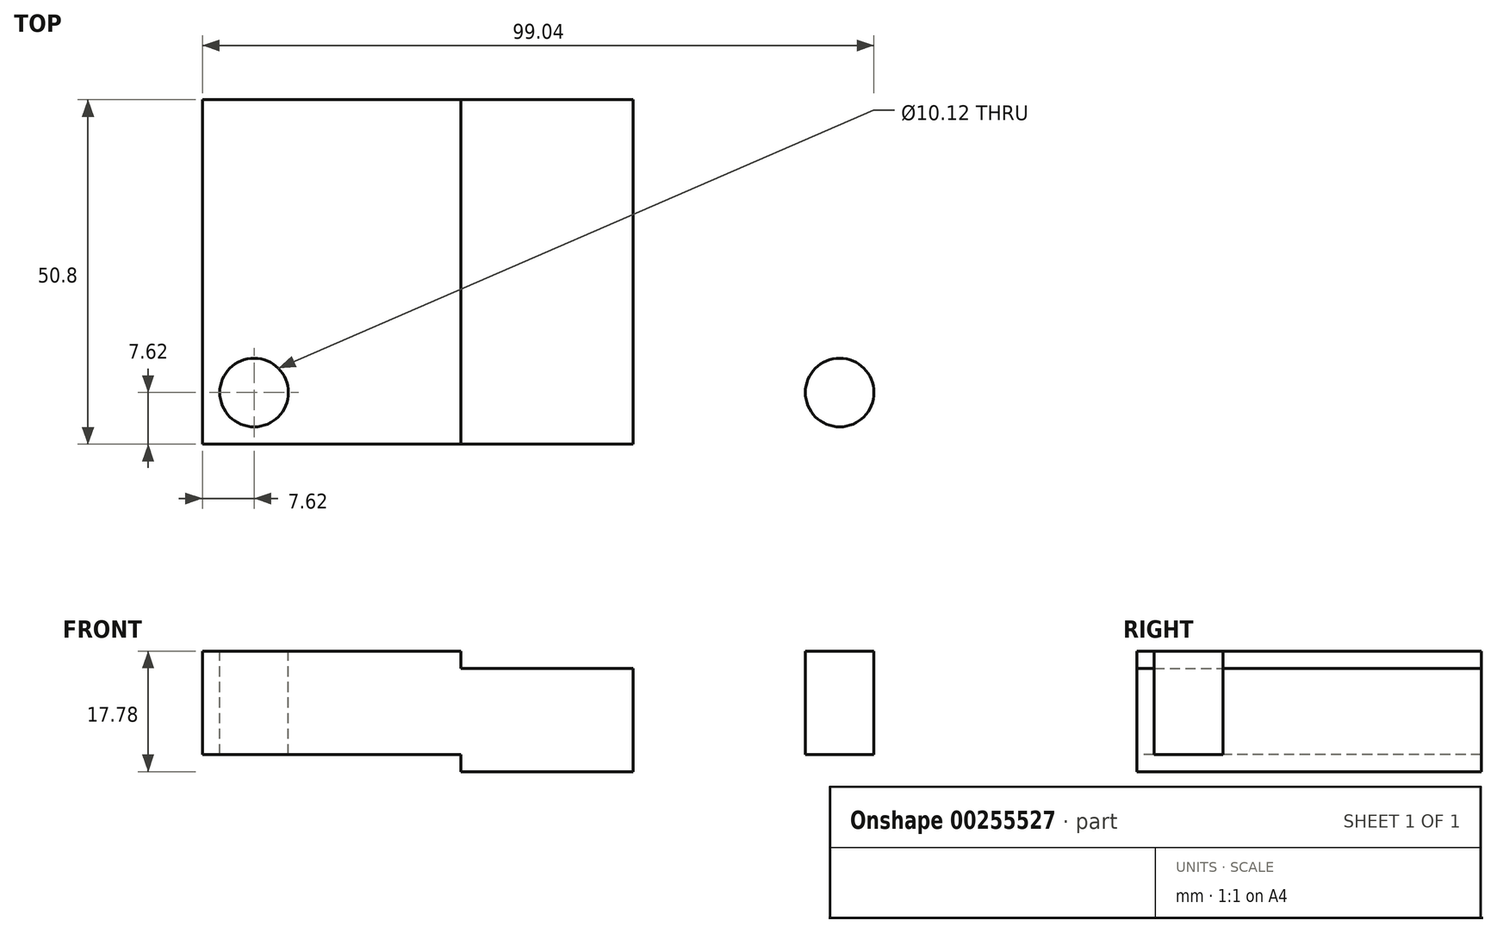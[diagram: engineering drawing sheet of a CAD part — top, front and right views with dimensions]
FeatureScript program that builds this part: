
annotation { "Feature Type Name" : "Feature", "Feature Type Description" : "" }
export const myFeature = defineFeature(function(context is Context, id is Id, definition is map)
    precondition{}
    {
        {
            var Q0;
            Q0=qCreatedBy(makeId("Top.planeOp"),FACE);
            var sketch = newSketch(context, id + "F0", { "sketchPlane" : qUnion([Q0])});
            skLineSegment(sketch, "E0.bottom", {"start": v(-50.8, 25.4) * mm, "end": v(50.8, 25.4) * mm});
            skLineSegment(sketch, "E0.top", {"start": v(-50.8, -25.4) * mm, "end": v(50.8, -25.4) * mm});
            skLineSegment(sketch, "E0.left", {"start": v(-50.8, 25.4) * mm, "end": v(-50.8, -25.4) * mm});
            skLineSegment(sketch, "E0.right", {"start": v(50.8, 25.4) * mm, "end": v(50.8, -25.4) * mm});
            skPoint(sketch, "E0.middle", {"position": v(0, 0) * mm});
            skLineSegment(sketch, "E1", {"start": v(-12.7, 25.4) * mm, "end": v(-12.7, -25.4) * mm});
            skLineSegment(sketch, "E2", {"start": v(12.7, 25.4) * mm, "end": v(12.7, -26.8) * mm});
            skSolve(sketch);
        }
        {
            var Q0;
            Q0 = qSketchRegion(id + "F0", true);
            extrude(context, id + "F1", {"entities" : qUnion([Q0]), "depth" : 12.7 * mm});
        }
        {
            var Q0;
            {var subQ0=sQuery(id+"F0.wireOp",EDGE,"E0.right");Q0=makeQuery(id+"F0.imprint","IMPRINT",FACE,{"disambiguationData":[TD([[makeQuery(id+"F0.imprint","IMPRINT",EDGE,{"derivedFrom":subQ0}),-1.0]])]});}
            var Q1;
            {var subQ0=sQuery(id+"F0.wireOp",EDGE,"E0.left");Q1=makeQuery(id+"F0.imprint","IMPRINT",FACE,{"disambiguationData":[TD([[makeQuery(id+"F0.imprint","IMPRINT",EDGE,{"derivedFrom":subQ0}),1.0]])]});}
            extrude(context, id + "F2", {"entities" : qUnion([Q0, Q1]), "operationType" : NewBodyOperationType.ADD, "depth" : 15.24 * mm});
        }
        {
            var Q0;
            Q0=makeQuery(id+"F1.opExtrude","CAP_FACE",FACE,{"disambiguationData":[OSD([sQuery(id+"F0.wireOp",EDGE,"E0.bottom"),sQuery(id+"F0.wireOp",EDGE,"E0.top"),sQuery(id+"F0.wireOp",EDGE,"E0.left"),sQuery(id+"F0.wireOp",EDGE,"E0.right")])],"isStart":true});
            var sketch = newSketch(context, id + "F3", { "sketchPlane" : qUnion([Q0])});
            skLineSegment(sketch, "E3", {"start": v(0, 0) * mm, "end": v(0, 25.4) * mm, "construction": true});
            skSolve(sketch);
        }
        {
            var Q0;
            Q0=sQuery(id+"F3.wireOp",VERTEX,"E3.end");
            var Q1;
            Q1=sQuery(id+"F3.wireOp",EDGE,"E3");
            cPlane(context, id + "F4", {"entities" : qUnion([Q0, Q1]), "cplaneType" : CPlaneType.LINE_POINT, "offset" : 25.4 * mm, "width" : 152.4 * mm, "height" : 152.4 * mm});
        }
        {
            var Q0;
            Q0=qCreatedBy(id+"F4.planeOp",FACE);
            var sketch = newSketch(context, id + "F5", { "sketchPlane" : qUnion([Q0])});
            skLineSegment(sketch, "E4", {"start": v(0, 0) * mm, "end": v(0, -2.54) * mm});
            skLineSegment(sketch, "E5", {"start": v(0, -2.54) * mm, "end": v(-12.7, -2.54) * mm});
            skLineSegment(sketch, "E6.MirrorCS", {"start": v(0, -2.54) * mm, "end": v(12.7, -2.54) * mm});
            skLineSegment(sketch, "E7", {"start": v(-12.7, -2.54) * mm, "end": v(-12.7, 0) * mm});
            skLineSegment(sketch, "E8", {"start": v(12.7, -2.54) * mm, "end": v(12.7, 0) * mm});
            skLineSegment(sketch, "E9", {"start": v(12.7, 0) * mm, "end": v(-12.7, 0) * mm});
            skSolve(sketch);
        }
        {
            var Q0;
            {var subQ0=sQuery(id+"F5.wireOp",EDGE,"E4");Q0=makeQuery(id+"F5.imprint","IMPRINT",FACE,{"disambiguationData":[TD([[makeQuery(id+"F5.imprint","IMPRINT",EDGE,{"derivedFrom":subQ0}),-1.0]])]});}
            var Q1;
            {var subQ0=sQuery(id+"F5.wireOp",EDGE,"E4");Q1=makeQuery(id+"F5.imprint","IMPRINT",FACE,{"disambiguationData":[TD([[makeQuery(id+"F5.imprint","IMPRINT",EDGE,{"derivedFrom":subQ0}),1.0]])]});}
            extrude(context, id + "F6", {"entities" : qUnion([Q0, Q1]), "operationType" : NewBodyOperationType.ADD, "oppositeDirection" : true, "depth" : 50.8 * mm});
        }
        {
            var Q0;
            Q0=makeQuery(id+"F2.opExtrude","CAP_FACE",FACE,{"disambiguationData":[OSD([sQuery(id+"F0.wireOp",EDGE,"E0.bottom"),sQuery(id+"F0.wireOp",EDGE,"E0.top"),sQuery(id+"F0.wireOp",EDGE,"E0.right"),sQuery(id+"F0.wireOp",EDGE,"E2")])],"isStart":false});
            var sketch = newSketch(context, id + "F7", { "sketchPlane" : qUnion([Q0])});
            skLineSegment(sketch, "E10", {"start": v(50.8, 25.4) * mm, "end": v(43.18, 25.4) * mm});
            skLineSegment(sketch, "E11", {"start": v(43.18, 25.4) * mm, "end": v(43.18, 17.78) * mm});
            skCircle(sketch, "E12", {"center": v(43.18, 17.78) * mm, "radius": 5.06 * mm});
            skCircle(sketch, "E13.MirrorC", {"center": v(43.18, -17.78) * mm, "radius": 5.06 * mm});
            skCircle(sketch, "E14.MirrorC", {"center": v(-43.18, -17.78) * mm, "radius": 5.06 * mm});
            skCircle(sketch, "E15.MirrorC", {"center": v(-43.18, 17.78) * mm, "radius": 5.06 * mm});
            skSolve(sketch);
        }
        {
            var Q0;
            Q0=makeQuery(id+"F7.imprint","IMPRINT",FACE,{"disambiguationData":[TD([[makeQuery(id+"F7.imprint","IMPRINT",EDGE,{"derivedFrom":sQuery(id+"F7.wireOp",EDGE,"E12")}),1.0]])]});
            var Q1;
            Q1=makeQuery(id+"F7.imprint","IMPRINT",FACE,{"disambiguationData":[TD([[makeQuery(id+"F7.imprint","IMPRINT",EDGE,{"derivedFrom":sQuery(id+"F7.wireOp",EDGE,"E13.MirrorC")}),-1.0]])]});
            var Q2;
            Q2=makeQuery(id+"F7.imprint","IMPRINT",FACE,{"disambiguationData":[TD([[makeQuery(id+"F7.imprint","IMPRINT",EDGE,{"derivedFrom":sQuery(id+"F7.wireOp",EDGE,"E15.MirrorC")}),-1.0]])]});
            var Q3;
            Q3=makeQuery(id+"F7.imprint","IMPRINT",FACE,{"disambiguationData":[TD([[makeQuery(id+"F7.imprint","IMPRINT",EDGE,{"derivedFrom":sQuery(id+"F7.wireOp",EDGE,"E14.MirrorC")}),1.0]])]});
            extrude(context, id + "F8", {"entities" : qUnion([Q0, Q1, Q2, Q3]), "operationType" : NewBodyOperationType.REMOVE, "endBound" : BoundingType.THROUGH_ALL, "oppositeDirection" : true, "depth" : 25.4 * mm});
        }
    });
